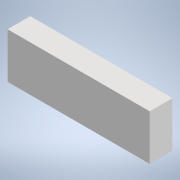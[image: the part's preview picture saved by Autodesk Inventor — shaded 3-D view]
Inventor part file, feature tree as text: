
AUTODESK INVENTOR PART (.ipt)
format: ipt  version: 2020 (Build 240168000, 168)  size: 89,088 bytes
history: native  units: in
note: dims shown in document units (in); Inventor stores cm internally (conversion verified against a paired STEP export)
features: reference x3, other x3, extrude x1, sketch x1
ambient origin geometry x8: Origin, YZ Plane, XZ Plane, XY Plane, X Axis, Y Axis, Z Axis, Center Point
bodies: Solid1 (feature_tree)
feature tree (8):
  extrude  "Extrusion1"  Depth=0.8in TaperAngle=0.0deg
  sketch  "Sketch1"  dims[d0=5.0in d1=0.8in d2=0.0in]
  reference  "Reference1"
  reference  "Reference2"
  reference  "Reference3"
  other  "<userpath>\Documents\Inventor\Drone\Assembly.iam"
  other  "Assembly.iam"
  other  "BatteryStopper:1"
